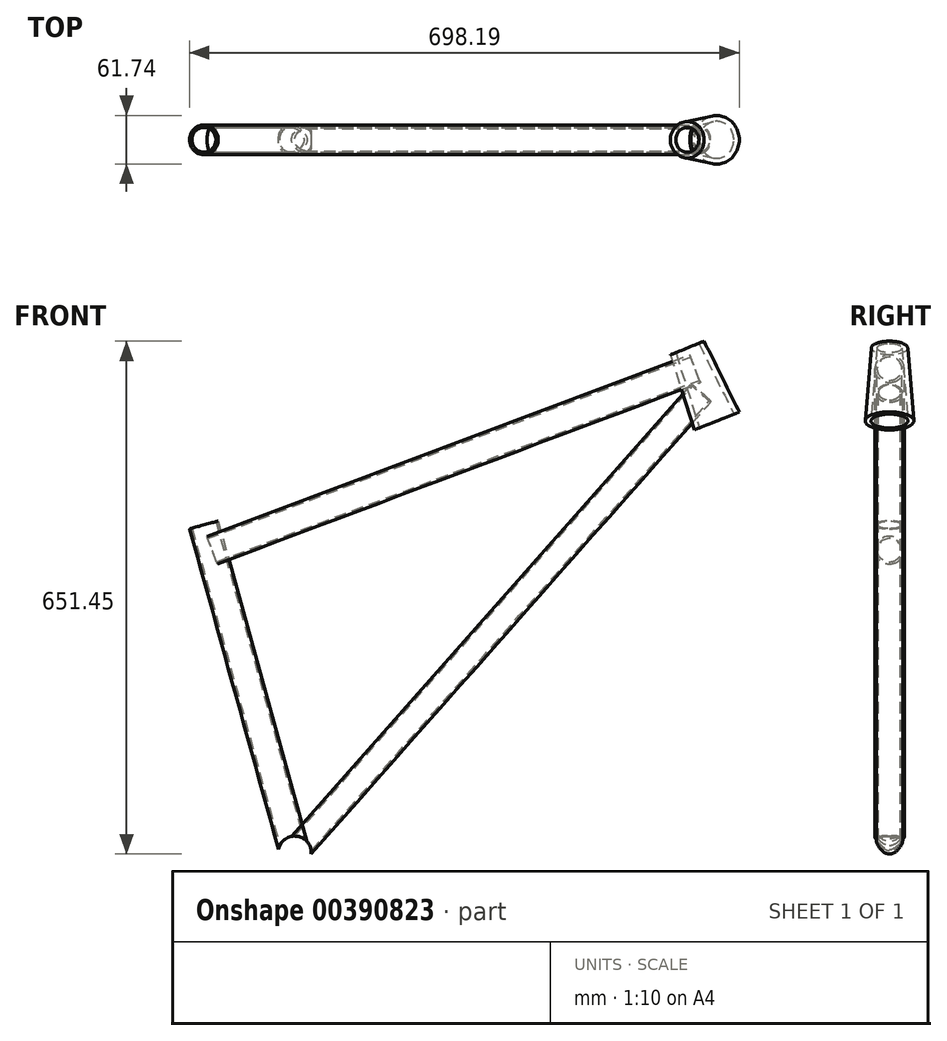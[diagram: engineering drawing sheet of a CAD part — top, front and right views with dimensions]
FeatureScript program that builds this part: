
annotation { "Feature Type Name" : "Feature", "Feature Type Description" : "" }
export const myFeature = defineFeature(function(context is Context, id is Id, definition is map)
    precondition{}
    {
        {
            var Q0;
            Q0=qCreatedBy(makeId("Front.planeOp"),FACE);
            var sketch = newSketch(context, id + "F0", { "sketchPlane" : qUnion([Q0])});
            skCircle(sketch, "E0", {"center": v(0, 0) * mm, "radius": 16.95 * mm});
            skCircle(sketch, "E1.0", {"center": v(0, 0) * mm, "radius": 20.95 * mm});
            skSolve(sketch);
        }
        {
            var Q0;
            Q0=qCreatedBy(makeId("Front.planeOp"),FACE);
            var sketch = newSketch(context, id + "F1", { "sketchPlane" : qUnion([Q0])});
            skLineSegment(sketch, "E2", {"start": v(0, 0) * mm, "end": v(-115.45, 416.29) * mm});
            skLineSegment(sketch, "E3.0", {"start": v(15.23, 4.22) * mm, "end": v(-100.22, 420.51) * mm});
            skLineSegment(sketch, "E4.0", {"start": v(18.12, 5.02) * mm, "end": v(-97.33, 421.31) * mm});
            skLineSegment(sketch, "E5", {"start": v(-100.22, 420.51) * mm, "end": v(-97.33, 421.31) * mm});
            skLineSegment(sketch, "E6", {"start": v(15.23, 4.22) * mm, "end": v(18.12, 5.02) * mm});
            skSolve(sketch);
        }
        {
            var Q0;
            Q0=makeQuery(id+"F1.imprint","IMPRINT",FACE,{"disambiguationData":[TD([[makeQuery(id+"F1.imprint","IMPRINT",EDGE,{"derivedFrom":sQuery(id+"F1.wireOp",EDGE,"E3.0")}),-1.0]])]});
            var Q1;
            Q1=sQuery(id+"F1.wireOp",EDGE,"E2");
            revolve(context, id + "F2", {"entities" : qUnion([Q0]), "axis" : qUnion([Q1]), "revolveType" : RevolveType.FULL});
        }
        {
            var Q0;
            Q0=qCreatedBy(makeId("Front.planeOp"),FACE);
            var sketch = newSketch(context, id + "F3", { "sketchPlane" : qUnion([Q0])});
            skCircle(sketch, "E7.0", {"center": v(0, 0) * mm, "radius": 20.95 * mm});
            skSolve(sketch);
        }
        {
            var Q0;
            Q0 = qSketchRegion(id + "F3", true);
            extrude(context, id + "F4", {"entities" : qUnion([Q0]), "operationType" : NewBodyOperationType.REMOVE, "endBound" : BoundingType.SYMMETRIC, "oppositeDirection" : true, "depth" : 68 * mm});
        }
        {
            var Q0;
            Q0=qCreatedBy(makeId("Front.planeOp"),FACE);
            var sketch = newSketch(context, id + "F5", { "sketchPlane" : qUnion([Q0])});
            skLineSegment(sketch, "E8", {"start": v(498.55, 641) * mm, "end": v(536.01, 548.28) * mm});
            skLineSegment(sketch, "E9", {"start": v(0, 0) * mm, "end": v(0, 65) * mm});
            skLineSegment(sketch, "E10", {"start": v(513.16, 646.9) * mm, "end": v(557.8, 557.08) * mm});
            skLineSegment(sketch, "E11", {"start": v(557.8, 557.08) * mm, "end": v(564.63, 559.84) * mm});
            skLineSegment(sketch, "E12", {"start": v(513.16, 646.9) * mm, "end": v(519.99, 649.66) * mm});
            skLineSegment(sketch, "E13", {"start": v(519.99, 649.66) * mm, "end": v(564.63, 559.84) * mm});
            skSolve(sketch);
        }
        {
            var Q0;
            Q0=makeQuery(id+"F5.imprint","IMPRINT",FACE,{"disambiguationData":[TD([[makeQuery(id+"F5.imprint","IMPRINT",EDGE,{"derivedFrom":sQuery(id+"F5.wireOp",EDGE,"E10")}),1.0]])]});
            var Q1;
            Q1=sQuery(id+"F5.wireOp",EDGE,"E8");
            revolve(context, id + "F6", {"entities" : qUnion([Q0]), "axis" : qUnion([Q1]), "revolveType" : RevolveType.FULL});
        }
        {
            var Q0;
            Q0=qCreatedBy(makeId("Front.planeOp"),FACE);
            var sketch = newSketch(context, id + "F7", { "sketchPlane" : qUnion([Q0])});
            skLineSegment(sketch, "E14", {"start": v(-111.44, 401.83) * mm, "end": v(501.94, 632.33) * mm});
            skLineSegment(sketch, "E15.0", {"start": v(-110.63, 398.93) * mm, "end": v(503, 629.53) * mm});
            skLineSegment(sketch, "E16", {"start": v(508.99, 614.9) * mm, "end": v(-106.41, 383.72) * mm});
            skLineSegment(sketch, "E17", {"start": v(-111.44, 401.83) * mm, "end": v(-110.63, 398.93) * mm});
            skLineSegment(sketch, "E18", {"start": v(501.94, 632.33) * mm, "end": v(503, 629.53) * mm});
            skSolve(sketch);
        }
        {
            var Q0;
            Q0=makeQuery(id+"F7.imprint","IMPRINT",FACE,{"disambiguationData":[TD([[makeQuery(id+"F7.imprint","IMPRINT",EDGE,{"derivedFrom":sQuery(id+"F7.wireOp",EDGE,"E14")}),-1.0]])]});
            var Q1;
            Q1=sQuery(id+"F7.wireOp",EDGE,"E16");
            revolve(context, id + "F8", {"entities" : qUnion([Q0]), "axis" : qUnion([Q1]), "revolveType" : RevolveType.FULL});
        }
        {
            var Q0;
            Q0=qCreatedBy(makeId("Front.planeOp"),FACE);
            var sketch = newSketch(context, id + "F9", { "sketchPlane" : qUnion([Q0])});
            skLineSegment(sketch, "E19", {"start": v(0, 0) * mm, "end": v(0, 65) * mm});
            skLineSegment(sketch, "E20", {"start": v(7.04, -17.43) * mm, "end": v(5.92, -14.65) * mm});
            skLineSegment(sketch, "E21", {"start": v(521.24, 589.55) * mm, "end": v(0, 0) * mm});
            skLineSegment(sketch, "E22", {"start": v(527.16, 574.9) * mm, "end": v(5.92, -14.65) * mm});
            skLineSegment(sketch, "E23", {"start": v(527.16, 574.9) * mm, "end": v(528.28, 572.12) * mm});
            skLineSegment(sketch, "E24", {"start": v(528.28, 572.12) * mm, "end": v(7.04, -17.43) * mm});
            skSolve(sketch);
        }
        {
            var Q0;
            Q0=makeQuery(id+"F9.imprint","IMPRINT",FACE,{"disambiguationData":[TD([[makeQuery(id+"F9.imprint","IMPRINT",EDGE,{"derivedFrom":sQuery(id+"F9.wireOp",EDGE,"E20")}),-1.0]])]});
            var Q1;
            Q1=sQuery(id+"F9.wireOp",EDGE,"E21");
            revolve(context, id + "F10", {"entities" : qUnion([Q0]), "axis" : qUnion([Q1]), "revolveType" : RevolveType.FULL});
        }
        {
            var Q0;
            Q0 = qSketchRegion(id + "F3", true);
            extrude(context, id + "F11", {"entities" : qUnion([Q0]), "operationType" : NewBodyOperationType.REMOVE, "endBound" : BoundingType.SYMMETRIC, "oppositeDirection" : true, "depth" : 68 * mm});
        }
    });
